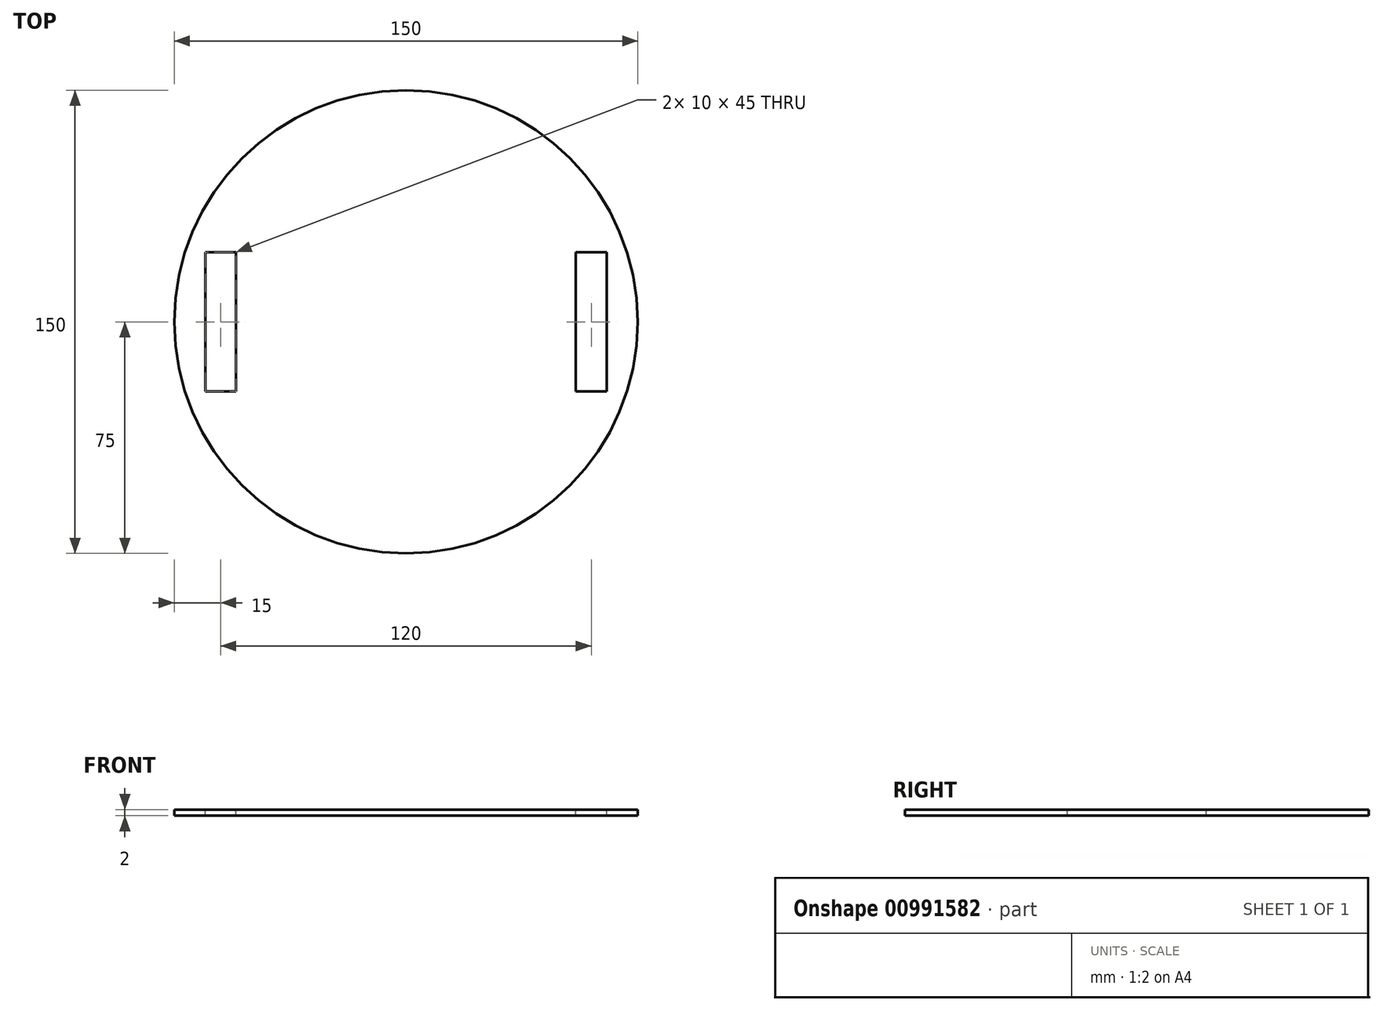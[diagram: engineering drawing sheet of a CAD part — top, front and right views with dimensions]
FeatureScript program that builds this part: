
annotation { "Feature Type Name" : "Feature", "Feature Type Description" : "" }
export const myFeature = defineFeature(function(context is Context, id is Id, definition is map)
    precondition{}
    {
        {
            var Q0;
            Q0=qCreatedBy(makeId("Top.planeOp"),FACE);
            var sketch = newSketch(context, id + "F0", { "sketchPlane" : qUnion([Q0])});
            skCircle(sketch, "E0", {"center": v(0, 0) * mm, "radius": 75 * mm});
            skSolve(sketch);
        }
        {
            var Q0;
            Q0=makeQuery(id+"F0.imprint","IMPRINT",FACE,{"disambiguationData":[TD([[makeQuery(id+"F0.imprint","IMPRINT",EDGE,{"derivedFrom":sQuery(id+"F0.wireOp",EDGE,"E0")}),1.0]])]});
            extrude(context, id + "F1", {"entities" : qUnion([Q0]), "depth" : 2 * mm, "offsetDistance" : 25 * mm});
        }
        {
            var Q0;
            Q0=makeQuery(id+"F1.opExtrude","CAP_FACE",FACE,{"disambiguationData":[OSD([sQuery(id+"F0.wireOp",EDGE,"E0")])],"isStart":false});
            var sketch = newSketch(context, id + "F2", { "sketchPlane" : qUnion([Q0])});
            skLineSegment(sketch, "E1", {"start": v(-75, 0) * mm, "end": v(0, 0) * mm});
            skLineSegment(sketch, "E2", {"start": v(0, 0) * mm, "end": v(75, 0) * mm});
            skLineSegment(sketch, "E3", {"start": v(0, 75) * mm, "end": v(0, -75) * mm});
            skSolve(sketch);
        }
        {
            var Q0;
            {var subQ0=sQuery(id+"F2.wireOp",EDGE,"E1");Q0=makeQuery(id+"F2.imprint","IMPRINT",FACE,{"disambiguationData":[TD([[makeQuery(id+"F2.imprint","IMPRINT",EDGE,{"derivedFrom":subQ0}),1.0]])]});}
            var sketch = newSketch(context, id + "F3", { "sketchPlane" : qUnion([Q0])});
            skLineSegment(sketch, "E4.bottom", {"start": v(-55, 22.5) * mm, "end": v(-65, 22.5) * mm});
            skLineSegment(sketch, "E4.top", {"start": v(-55, -22.5) * mm, "end": v(-65, -22.5) * mm});
            skLineSegment(sketch, "E4.left", {"start": v(-55, 22.5) * mm, "end": v(-55, -22.5) * mm});
            skLineSegment(sketch, "E4.right", {"start": v(-65, 22.5) * mm, "end": v(-65, -22.5) * mm});
            skPoint(sketch, "E4.middle", {"position": v(-60, 0) * mm});
            skLineSegment(sketch, "E5.MirrorCS", {"start": v(55, 22.5) * mm, "end": v(55, -22.5) * mm});
            skLineSegment(sketch, "E6.MirrorCS", {"start": v(55, 22.5) * mm, "end": v(65, 22.5) * mm});
            skLineSegment(sketch, "E7.MirrorCS", {"start": v(65, 22.5) * mm, "end": v(65, -22.5) * mm});
            skLineSegment(sketch, "E8.MirrorCS", {"start": v(55, -22.5) * mm, "end": v(65, -22.5) * mm});
            skSolve(sketch);
        }
        {
            var Q0;
            {var subQ0=sQuery(id+"F3.wireOp",EDGE,"E4.top");Q0=makeQuery(id+"F3.imprint","IMPRINT",FACE,{"disambiguationData":[TD([[makeQuery(id+"F3.imprint","IMPRINT",EDGE,{"derivedFrom":subQ0}),-1.0]])]});}
            var Q1;
            {var subQ0=sQuery(id+"F3.wireOp",EDGE,"E4.bottom");Q1=makeQuery(id+"F3.imprint","IMPRINT",FACE,{"disambiguationData":[TD([[makeQuery(id+"F3.imprint","IMPRINT",EDGE,{"derivedFrom":subQ0}),1.0]])]});}
            var Q2;
            Q2=makeQuery(id+"F3.imprint","IMPRINT",FACE,{"disambiguationData":[TD([[makeQuery(id+"F3.imprint","IMPRINT",EDGE,{"derivedFrom":sQuery(id+"F3.wireOp",EDGE,"E5.MirrorCS")}),1.0]])]});
            extrude(context, id + "F4", {"entities" : qUnion([Q0, Q1, Q2]), "operationType" : NewBodyOperationType.REMOVE, "oppositeDirection" : true, "depth" : 25 * mm, "offsetDistance" : 25 * mm});
        }
    });
